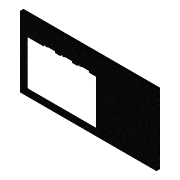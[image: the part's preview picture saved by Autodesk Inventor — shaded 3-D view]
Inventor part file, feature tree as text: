
AUTODESK INVENTOR PART (.ipt)
format: ipt  version: 2019.4 (Build 234330000, 330)  size: 214,528 bytes
history: native  units: mm
features: reference x9, sketch x5, extrude x4, other x4, hole x2, projected_geometry x2, fillet x1, pattern_linear x1
ambient origin geometry x8: Origin, YZ Plane, XZ Plane, XY Plane, X Axis, Y Axis, Z Axis, Center Point
bodies: Solid1 (feature_tree)
feature tree (28):
  extrude  "Extrusion1"  Depth=7.0mm
  extrude  "Extrusion7"  TaperAngle=0.0deg  [1 undecoded]
  hole  "Hole5"  [1 undecoded]
  fillet  "Fillet2"  Radius=6.0mm
  extrude  "Extrusion9"  Depth=1.5mm
  pattern_linear  "Rectangular Pattern2"  Spacing1=27.925268mm  [1 undecoded]
  extrude  "Extrusion10"  Depth=3.0mm TaperAngle=0.0deg
  sketch  "Sketch14"  dims[d88=2.0mm d89=1.5mm]
  hole  "Hole6"  [1 undecoded]
  sketch  "Sketch1"  dims[d1=2.0mm d2=0.0mm d73=7.0mm]
  projected_geometry  "Projected Loop10"
  sketch  "Sketch12"  dims[d74=4.0mm d75=0.0mm d78=0.0mm]
  projected_geometry  "Projected Loop11"
  sketch  "Sketch13"  dims[d79=4.3mm d80=6.0mm d81=4.0mm d82=2.0mm d83=90.0deg d84=8.0mm d85=20.594885mm d86=5.0mm d87=6.0mm]
  reference  "Reference34"
  reference  "Reference35"
  reference  "Reference36"
  reference  "Reference37"
  reference  "Reference38"
  reference  "Reference39"
  reference  "Reference40"
  reference  "Reference41"
  reference  "Reference42"
  sketch  "Sketch15"  dims[d90=1.5mm d91=27.925268mm d92=3.0mm d93=0.0mm d94=30.0mm d96=30.0mm d97=3.0mm d98=0.0mm d99=2.8mm d100=6.0mm d101=6.0mm d102=5.0mm d103=90.0deg d104=8.0mm d105=20.594885mm]
  other  "Assembly_Opentrons_Imagingunit_v3.iam"
  other  "00_MTP_96-welplate:1"
  other  "00_arduino uno:1"
  other  "00_Raspi:1"
note: 4 required parameter values undecoded (feature->parameter linkage not recoverable at this tier; creation-order binding heuristic only, values carry confidence <= 0.55)
